# Revit family: Desk_Accessories-Teknion-BAMPM_Peninsula_Modesty_Panel_Metal-R2018
name_source: partatom
category: Furniture
revit_build: Autodesk Revit 2018 (Build: 20170223_1515(x64)
units: mm (PartAtom-declared; Revit-internal decimal feet)

## family parameters
Always vertical = Yes
Cut with Voids When Loaded = No
OmniClass Number = 23.40.20.00
OmniClass Title = General Furniture and Specialties
Room Calculation Point = No
Shared = Yes
Work Plane-Based = No

## types (2) — shared parameters
Assembly Code = E2020200
Manufacturer = Teknion
Manufacturer Fax = 416.661.4586
Part Number = BAMPM
Product Documentation Link = https://www.teknion.com
Product Line = Expansion Casegoods
Product Page URL = https://www.teknion.com
Series = Expansion Casegoods
Sustainability Data = https://www.teknion.com
URL = www.teknion.com
Unit Weight URL = http://www.teknion.com
Warranty = http://www.teknion.com

## per-type parameters (varying)
| type | Description | Dual Leg | Model |
| Dual-Leg Peninsula Style, Half Modesty Panel Height | Peninsula Modesty Panel – Metal, Dual-Leg Peninsula Style, Half Modesty Panel Height, Solid Style | Yes | BAMPMDH__N |
| Mono-Leg or Base Peninsula Style, Half Modesty Panel Height | Peninsula Modesty Panel – Metal, Mono-Leg or Base Peninsula Style, Half Modesty Panel Height, Solid Style | No | BAMPMMH__N |

## geometry (parser evidence)
native form markers: Sweep x3
no freeform markers — native parametric forms only
